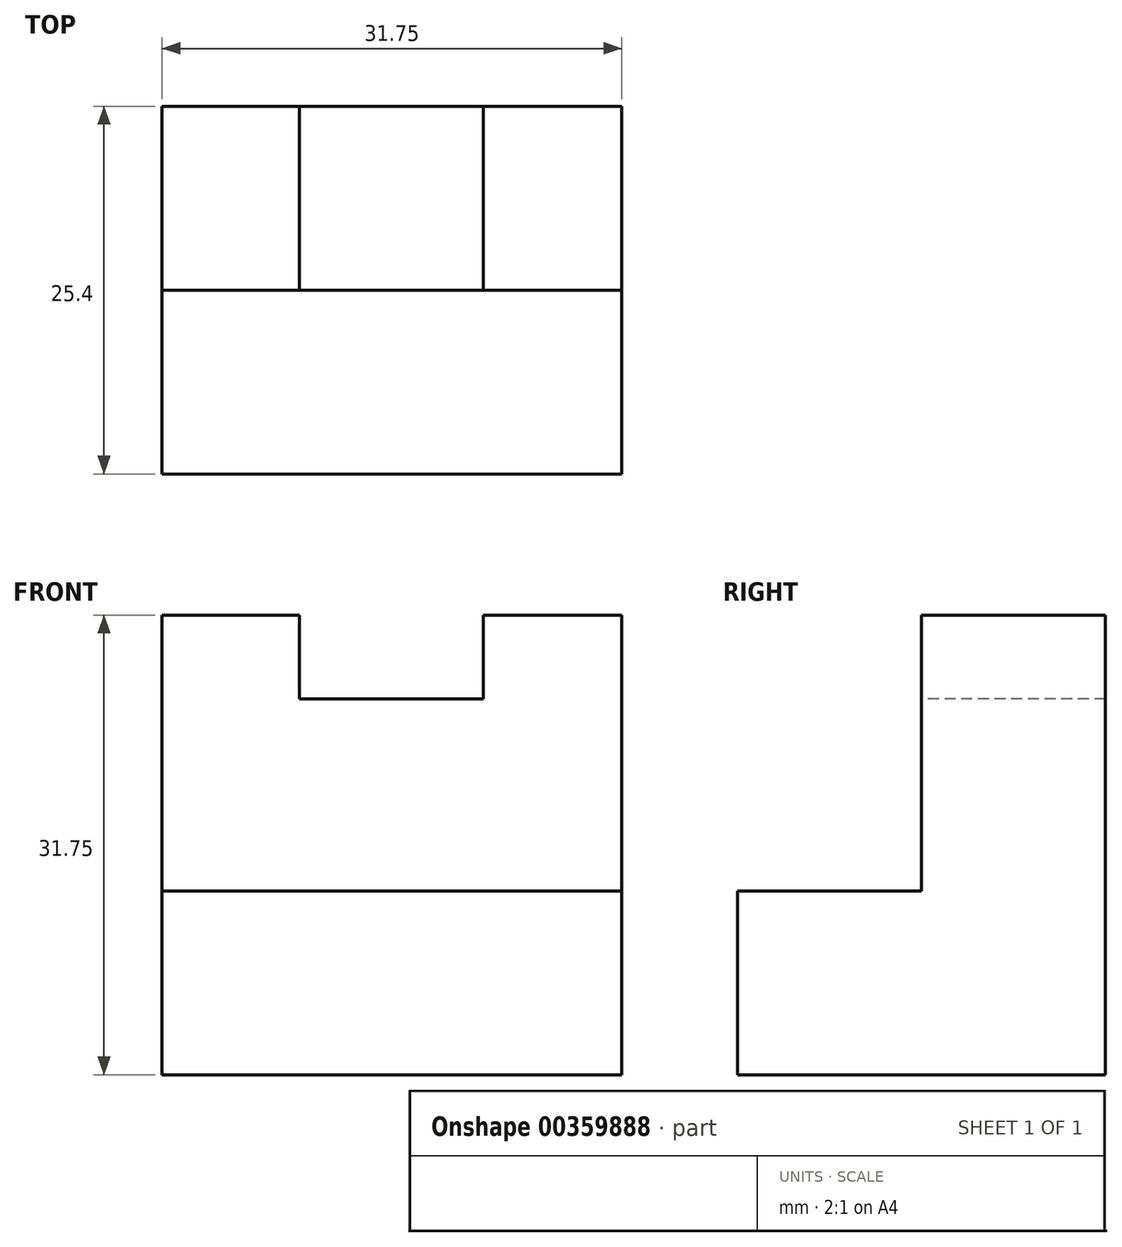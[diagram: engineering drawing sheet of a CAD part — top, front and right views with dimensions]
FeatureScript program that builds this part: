
annotation { "Feature Type Name" : "Feature", "Feature Type Description" : "" }
export const myFeature = defineFeature(function(context is Context, id is Id, definition is map)
    precondition{}
    {
        {
            var Q0;
            Q0=qCreatedBy(makeId("Right.planeOp"),FACE);
            var sketch = newSketch(context, id + "F0", { "sketchPlane" : qUnion([Q0])});
            skLineSegment(sketch, "E0", {"start": v(0, 0) * mm, "end": v(25.4, 0) * mm});
            skLineSegment(sketch, "E1", {"start": v(25.4, 0) * mm, "end": v(25.4, 31.75) * mm});
            skLineSegment(sketch, "E2", {"start": v(25.4, 31.75) * mm, "end": v(12.7, 31.75) * mm});
            skLineSegment(sketch, "E3", {"start": v(12.7, 31.75) * mm, "end": v(12.7, 12.7) * mm});
            skLineSegment(sketch, "E4", {"start": v(12.7, 12.7) * mm, "end": v(0, 12.7) * mm});
            skLineSegment(sketch, "E5", {"start": v(0, 12.7) * mm, "end": v(0, 0) * mm});
            skSolve(sketch);
        }
        {
            var Q0;
            Q0 = qSketchRegion(id + "F0", true);
            extrude(context, id + "F1", {"entities" : qUnion([Q0]), "depth" : 31.75 * mm});
        }
        {
            var Q0;
            Q0=qCreatedBy(makeId("Front.planeOp"),FACE);
            var sketch = newSketch(context, id + "F2", { "sketchPlane" : qUnion([Q0])});
            skLineSegment(sketch, "E6", {"start": v(9.48, 32.3) * mm, "end": v(9.48, 25.96) * mm});
            skLineSegment(sketch, "E7", {"start": v(9.48, 25.96) * mm, "end": v(22.18, 25.96) * mm});
            skLineSegment(sketch, "E8", {"start": v(22.18, 25.96) * mm, "end": v(22.18, 32.3) * mm});
            skLineSegment(sketch, "E9", {"start": v(22.18, 32.3) * mm, "end": v(9.48, 32.3) * mm});
            skSolve(sketch);
        }
        {
            var Q0;
            Q0 = qSketchRegion(id + "F2", true);
            extrude(context, id + "F3", {"entities" : qUnion([Q0]), "operationType" : NewBodyOperationType.REMOVE, "oppositeDirection" : true, "depth" : 25.4 * mm});
        }
        {
            var Q0;
            Q0 = qSketchRegion(id + "F2", true);
            extrude(context, id + "F4", {"entities" : qUnion([Q0]), "operationType" : NewBodyOperationType.REMOVE, "oppositeDirection" : true, "depth" : 25.4 * mm});
        }
    });
